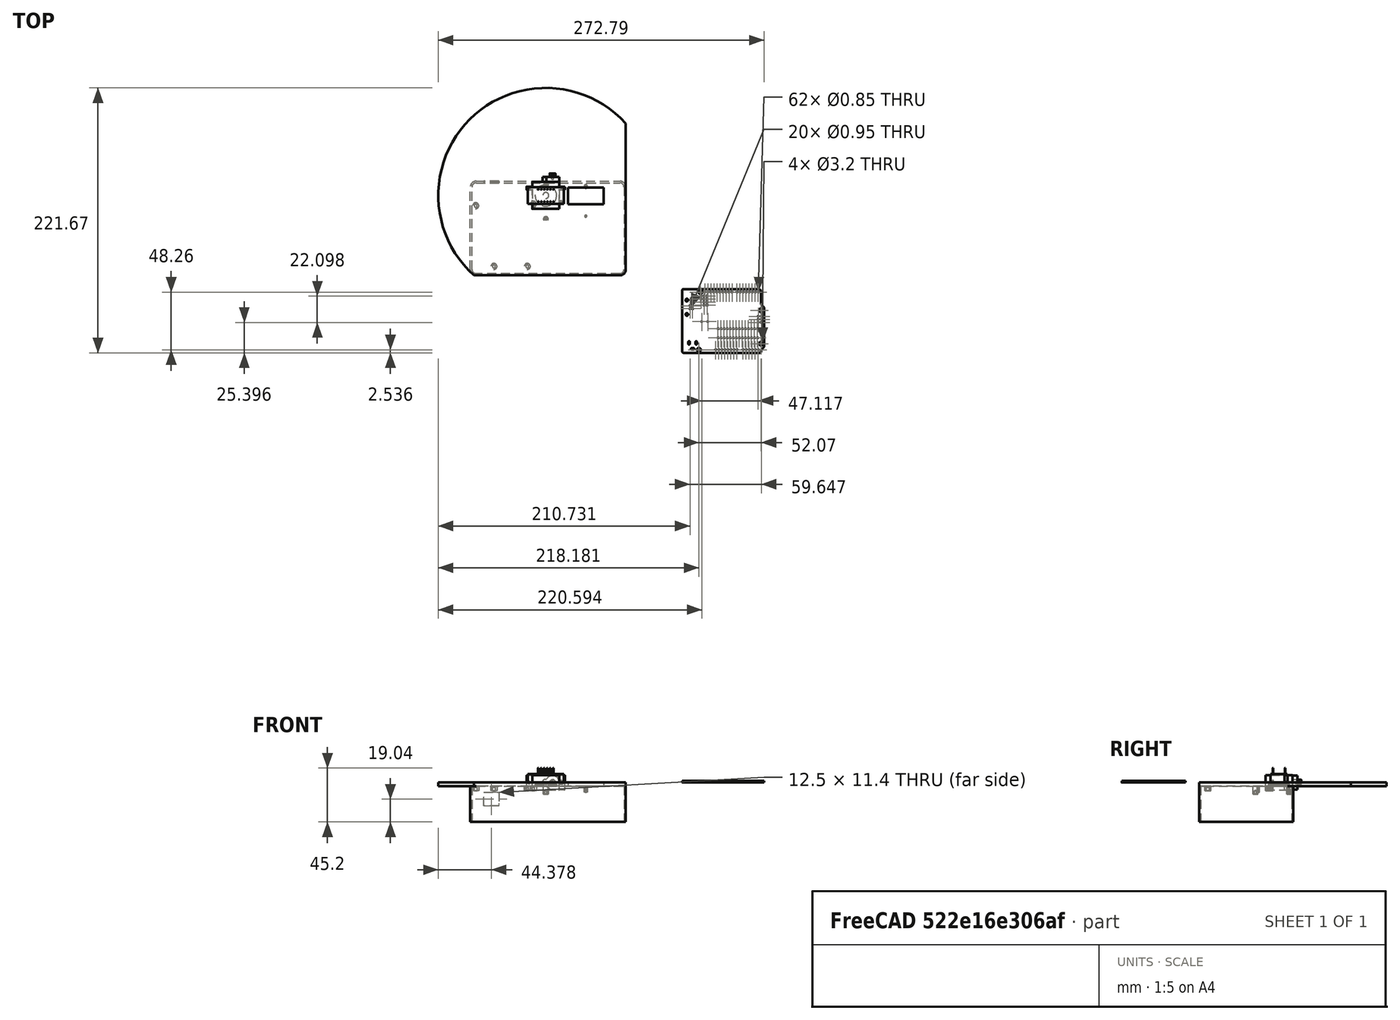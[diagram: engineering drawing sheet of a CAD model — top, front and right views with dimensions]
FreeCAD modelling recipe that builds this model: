
FCSTD DOCUMENT  (FreeCAD 1.0RUnknown)
Label: shell.FCStd.bak
License: All rights reserved
LicenseURL: https://en.wikipedia.org/wiki/All_rights_reserved
objects: App::FeaturePython×9, Sketcher::SketchObject×7, PartDesign::Pad×6, App::Link×4, Part::Feature×3, PartDesign::Hole×3, PartDesign::Pocket×2, App::Part×1, Assembly::JointGroup×1, Assembly::AssemblyObject×1, PartDesign::Body×1
note: 51 computed .brp shape members not serialized (recipe doc carries the construction recipe); baked Part::Feature solids carry a one-line shape summary decoded from their .brp

FEATURE [Sketcher::SketchObject] Sketch
  ArcFitTolerance = 1e-06
  AttachmentSupport = -> [XY_Plane]
  FullyConstrained = true
  MakeInternals = false
  MapMode = 5
  sketch-geometry (14):
    g0: LineSegment StartX=18.4415 StartY=6.5 StartZ=0 EndX=18.4415 EndY=-7.5 EndZ=0
    g1: LineSegment StartX=18.4415 StartY=-7.5 StartZ=0 EndX=48.4415 EndY=-7.5 EndZ=0
    g2: LineSegment StartX=48.4415 StartY=-7.5 StartZ=0 EndX=48.4415 EndY=6.5 EndZ=0
    g3: LineSegment StartX=48.4415 StartY=6.5 StartZ=0 EndX=18.4415 EndY=6.5 EndZ=0
    g4: GeomPoint [constr] X=33.4415 Y=-0.5 Z=0
    g5: ArcOfCircle CenterX=0 CenterY=0 CenterZ=0 NormalX=0 NormalY=0 NormalZ=1 AngleXU=0 Radius=90 StartAngle=0.733038 EndAngle=3.97935
    g6: Circle CenterX=0 CenterY=0 CenterZ=0 NormalX=0 NormalY=0 NormalZ=1 AngleXU=0 Radius=2.5
    g7: LineSegment [constr] StartX=0 StartY=0 StartZ=0 EndX=66.883 EndY=60.2218 EndZ=0
    g8: LineSegment [constr] StartX=0 StartY=0 StartZ=0 EndX=-60.2218 EndY=-66.883 EndZ=0
    g9: LineSegment StartX=66.883 StartY=60.2218 StartZ=0 EndX=66.883 EndY=-61.883 EndZ=0
    g10: LineSegment StartX=61.883 StartY=-66.883 StartZ=0 EndX=-60.2218 EndY=-66.883 EndZ=0
    g11: ArcOfCircle CenterX=61.883 CenterY=-61.883 CenterZ=0 NormalX=0 NormalY=0 NormalZ=1 AngleXU=0 Radius=5 StartAngle=4.71239 EndAngle=6.28319
    g12: LineSegment [constr] StartX=48.4415 StartY=3.78 StartZ=0 EndX=66.883 EndY=3.78 EndZ=0
    g13: LineSegment [constr] StartX=0 StartY=0 StartZ=0 EndX=18.4415 EndY=0 EndZ=0
  constraints (37):
    c: Coincident(g0,g1)
    c: Coincident(g1,g2)
    c: Coincident(g2,g3)
    c: Coincident(g3,g0)
    c: Vertical(g2)
    c: Horizontal(g1)
    c: Horizontal(g3)
    c: Symmetric(g2,g0,g4)
    c: DistanceX(g1,g1) = 30
    c: DistanceY(g2,g2) = 14
    c: Radius(g5) = 90
    c: Coincident(g5,g-1)
    c: Coincident(g6,g5)
    c: Diameter(g6) = 5
    c: Coincident(g7,g5)
    c: Coincident(g8,g5)
    c: Angle(g8,g-1,g5) = 2.30383
    c: Vertical(g9)
    c: Horizontal(g10)
    c: Angle(g-1,g7) = 0.733038
    c: Tangent(g9,g11) = 1.5708
    c: Tangent(g10,g11) = 1.5708
    c: Radius(g11) = 5
    c: Coincident(g5,g8)
    c: Coincident(g5,g7)
    c: Coincident(g9,g5)
    c: Coincident(g10,g5)
    c: PointOnObject(g12,g9)
    c: PointOnObject(g12,g2)
    c: DistanceY(g-1,g12) = 3.78
    c: Horizontal(g12,g12)
    c: Coincident(g13,g5)
    c: Vertical(g13,g0)
    c: PointOnObject(g13,g-1)
    c: Equal(g12,g13)
    c: Perpendicular(g0,g1)
    c: DistanceY(g-1,g4) = -0.5
FEATURE [PartDesign::Pad] Pad
  Direction = (0,0,1)
  Length = 3
  Length2 = 10
  Profile = -> Sketch
  ReferenceAxis = -> Sketch [N_Axis]
  Refine = true
  Reversed = true
  Suppressed = false
  Type = 0
FEATURE [Sketcher::SketchObject] Sketch001
  ArcFitTolerance = 1e-06
  FullyConstrained = true
  MakeInternals = false
  MapMode = 5
  Placement = pos=(0,0,-3) rot=(1,0,0;3.14159rad)
  sketch-geometry (1):
    g0: Circle CenterX=0 CenterY=0 CenterZ=0 NormalX=0 NormalY=0 NormalZ=1 AngleXU=0 Radius=9
  constraints (2):
    c: Diameter(g0) = 18
    c: Coincident(g0,g-1)
FEATURE [Sketcher::SketchObject] Sketch003
  ArcFitTolerance = 1e-06
  FullyConstrained = true
  MakeInternals = false
  MapMode = 5
  Placement = pos=(0,0,-3) rot=(1,0,0;3.14159rad)
  sketch-geometry (3):
    g0: Circle CenterX=1e-16 CenterY=19.72 CenterZ=0 NormalX=0 NormalY=0 NormalZ=1 AngleXU=0 Radius=2
    g1: Circle CenterX=0 CenterY=-8.53 CenterZ=0 NormalX=0 NormalY=0 NormalZ=1 AngleXU=0 Radius=2
    g2: LineSegment [constr] StartX=1e-16 StartY=19.72 StartZ=0 EndX=0 EndY=-8.53 EndZ=0
  constraints (8):
    c: Diameter(g0) = 4
    c: Diameter(g1) = 4
    c: Distance(g0,g1) = 28.25
    c: Distance(g1,g-1) = 8.53
    c: DistanceX(g1,g-1) = 0
    c: Coincident(g2,g0)
    c: Coincident(g2,g1)
    c: PointOnObject(g-1,g2)
FEATURE [PartDesign::Pocket] Pocket001
  BaseFeature = -> Pad
  Direction = (0,0,1)
  Length = 1.5
  Length2 = 5
  Profile = -> Sketch001
  ReferenceAxis = -> Sketch001 [N_Axis]
  Refine = true
  Suppressed = false
  Type = 0
FEATURE [Sketcher::SketchObject] Sketch002
  ArcFitTolerance = 1e-06
  AttachmentSupport = -> [Pocket001]
  ExternalGeometry = -> [Pocket001]
  FullyConstrained = true
  MakeInternals = false
  MapMode = 5
  Placement = pos=(0,0,-3) rot=(1,0,0;3.14159rad)
  sketch-geometry (5):
    g0: Circle CenterX=-43.4418 CenterY=59.423 CenterZ=0 NormalX=0 NormalY=0 NormalZ=1 AngleXU=0 Radius=2.5
    g1: Circle CenterX=-15.5018 CenterY=59.423 CenterZ=0 NormalX=0 NormalY=0 NormalZ=1 AngleXU=0 Radius=2.5
    g2: Circle CenterX=-10.4218 CenterY=7.35303 CenterZ=0 NormalX=0 NormalY=0 NormalZ=1 AngleXU=0 Radius=2.5
    g3: Circle CenterX=-58.6818 CenterY=8.62303 CenterZ=0 NormalX=0 NormalY=0 NormalZ=1 AngleXU=0 Radius=2.5
    g4: GeomPoint X=-61.2218 Y=-6.61697 Z=0
  constraints (14):
    c: Equal(g1,g0)
    c: Equal(g0,g3)
    c: Equal(g3,g2)
    c: Diameter(g3) = 5
    c: DistanceY(g4,g3) = 15.24
    c: DistanceY(g4,g0) = 66.04
    c: Horizontal(g0,g1)
    c: DistanceX(g4,g3) = 2.54
    c: DistanceX(g4,g2) = 50.8
    c: DistanceX(g4,g0) = 17.78
    c: DistanceX(g4,g1) = 45.72
    c: DistanceX(g4,g-3) = 1
    c: DistanceY(g4,g-3) = 73.5
    c: DistanceY(g4,g2) = 13.97
FEATURE [PartDesign::Pad] Pad005
  BaseFeature = -> Pocket001
  Direction = (0,0,-1)
  Length = 4
  Length2 = 10
  Profile = -> Sketch002
  ReferenceAxis = -> Sketch002 [N_Axis]
  Refine = true
  Suppressed = false
  Type = 0
FEATURE [PartDesign::Pad] Pad002
  BaseFeature = -> Pad005
  Direction = (0,-1e-16,-1)
  Length = 6.75
  Length2 = 10
  Profile = -> Sketch003
  ReferenceAxis = -> Sketch003 [N_Axis]
  Refine = true
  Suppressed = false
  Type = 0
FEATURE [Sketcher::SketchObject] Sketch005
  ArcFitTolerance = 1e-06
  ExternalGeometry = -> [Sketch002]
  FullyConstrained = true
  MakeInternals = false
  MapMode = 5
  Placement = pos=(0,12.03,0) rot=(0,0.707107,0.707107;3.14159rad)
  sketch-geometry (4):
    g0: LineSegment StartX=51.8718 StartY=-19.66 StartZ=0 EndX=51.8718 EndY=-8.26 EndZ=0
    g1: LineSegment StartX=51.8718 StartY=-8.26 StartZ=0 EndX=39.3718 EndY=-8.26 EndZ=0
    g2: LineSegment StartX=39.3718 StartY=-8.26 StartZ=0 EndX=39.3718 EndY=-19.66 EndZ=0
    g3: LineSegment StartX=39.3718 StartY=-19.66 StartZ=0 EndX=51.8718 EndY=-19.66 EndZ=0
  constraints (12):
    c: Coincident(g0,g1)
    c: Coincident(g1,g2)
    c: Coincident(g2,g3)
    c: Coincident(g3,g0)
    c: Vertical(g0)
    c: Vertical(g2)
    c: Horizontal(g1)
    c: Horizontal(g3)
    c: DistanceY(g1,g-3) = 5.26
    c: DistanceX(g0,g-3) = 9.35
    c: DistanceX(g1,g1) = 12.5
    c: DistanceY(g2,g2) = 11.4
FEATURE [App::Link] shell  label="shell001"
  LinkedObject = -> Body
FEATURE [App::FeaturePython] GroundedJoint  # Assembly grounded joint (typed FeaturePython)
  ObjectToGround = -> shell
FEATURE [Part::Feature] Part__Feature  label="SG90-SERVO"
  shape: bbox 32.25 x 29.75 x 12.5 mm, 92 faces (baked)
FEATURE [Part::Feature] Part__Feature001  label="Corps"
  shape: bbox 30 x 14 x 12.2 mm, 30 faces (baked)
FEATURE [Part::Feature] Part__Feature002  label="UNO-TH_Rev3e_PCB"
  shape: bbox 68.58 x 53.34 x 1.51 mm, 119 faces (baked)
FEATURE [App::Part] UNO_TH_Rev3e_1  label="UNO-TH_Rev3e 1"
  Group = -> [Part__Feature002]
  Origin = -> Origin002
FEATURE [App::Link] SG90_SERVO  label="SG90-SERVO001"
  LinkPlacement = pos=(-2.1e-15,-5.595,-17) rot=(0.57735,0.57735,0.57735;2.0944rad)
  LinkedObject = -> Part__Feature
  Placement = pos=(-2.1e-15,-5.595,-17) rot=(0.57735,0.57735,0.57735;2.0944rad)
FEATURE [App::Link] Corps  label="Corps001"
  LinkPlacement = pos=(33.4415,-0.5,0) rot=(1,0,0;3.14159rad)
  LinkedObject = -> Part__Feature001
  Placement = pos=(33.4415,-0.5,0) rot=(1,0,0;3.14159rad)
FEATURE [App::Link] UNO_TH_Rev3e_PCB  label="UNO-TH_Rev3e_PCB001"
  LinkPlacement = pos=(-139.439,120.908,-7) rot=(-0.706879,0.707335,0;3.14159rad)
  LinkedObject = -> Part__Feature002
  Placement = pos=(-139.439,120.908,-7) rot=(-0.706879,0.707335,0;3.14159rad)
FEATURE [App::FeaturePython] Joint  label="Longueur"  # Assembly joint (typed FeaturePython)
  Activated = true
  AngleMax = 0
  AngleMin = 0
  Detach1 = false
  Detach2 = false
  Distance = 0
  Distance2 = 0
  EnableAngleMax = false
  EnableAngleMin = false
  EnableLengthMax = false
  EnableLengthMin = false
  JointType = 5 (Distance)
  LengthMax = 0
  LengthMin = 0
  Placement1 = pos=(-13.6729,7.25,-7.24e-14) rot=(0,-0.707107,-0.707107;3.14159rad)
  Placement2 = pos=(-2e-16,-19.72,-9.75) rot=(0,0,1;1.5708rad)
  Reference1 = -> Assembly [SG90_SERVO.Face3,SG90_SERVO.Face3]
  Reference2 = -> Assembly [shell.Face47,shell.Face47]
FEATURE [App::FeaturePython] Joint001  label="Pivotglissant"  # Assembly joint (typed FeaturePython)
  Activated = true
  AngleMax = 0
  AngleMin = 0
  Detach1 = false
  Detach2 = false
  Distance = 0
  Distance2 = 0
  EnableAngleMax = false
  EnableAngleMin = false
  EnableLengthMax = false
  EnableLengthMin = false
  JointType = 2 (Cylindrical)
  LengthMax = 0
  LengthMin = 0
  Placement1 = pos=(-14.125,4.75,3.1e-15) rot=(-0.186157,-0.694747,-0.694747;2.77349rad)
  Placement2 = pos=(1e-16,-19.72,-9.75) rot=(0,1,0;3.14159rad)
  Reference1 = -> Assembly [SG90_SERVO.Edge57,SG90_SERVO.Edge57]
  Reference2 = -> Assembly [shell.Edge128,shell.Edge128]
FEATURE [App::FeaturePython] Joint002  label="Parallèle"  # Assembly joint (typed FeaturePython)
  Activated = true
  AngleMax = 0
  AngleMin = 0
  Detach1 = false
  Detach2 = false
  Distance = 0
  Distance2 = 0
  EnableAngleMax = false
  EnableAngleMin = false
  EnableLengthMax = false
  EnableLengthMin = false
  JointType = 6 (Parallel)
  LengthMax = 0
  LengthMin = 0
  Placement1 = pos=(16.125,6,3) rot=(-0.57735,-0.57735,-0.57735;4.18879rad)
  Placement2 = pos=(3.75822,10.53,-18.1663) rot=(1,0,0;1.5708rad)
  Reference1 = -> Assembly [SG90_SERVO.Face24,SG90_SERVO.Face24]
  Reference2 = -> Assembly [shell.Face21,shell.Face21]
FEATURE [App::FeaturePython] Joint003  label="Longueur001"  # Assembly joint (typed FeaturePython)
  Activated = true
  AngleMax = 0
  AngleMin = 0
  Detach1 = false
  Detach2 = false
  Distance = 0
  Distance2 = 0
  EnableAngleMax = false
  EnableAngleMin = false
  EnableLengthMax = false
  EnableLengthMin = false
  JointType = 5 (Distance)
  LengthMax = 0
  LengthMin = 0
  Placement2 = pos=(15,2e-16,3.6) rot=(-0.57735,-0.57735,0.57735;2.0944rad)
  Reference1 = -> Assembly [shell.?Face13,shell.?Face13]
  Reference2 = -> Assembly [Corps.Face3,Corps.Face3]
FEATURE [App::FeaturePython] Joint004  label="Longueur002"  # Assembly joint (typed FeaturePython)
  Activated = true
  AngleMax = 0
  AngleMin = 0
  Detach1 = false
  Detach2 = false
  Distance = 0
  Distance2 = 0
  EnableAngleMax = false
  EnableAngleMin = false
  EnableLengthMax = false
  EnableLengthMin = false
  JointType = 5 (Distance)
  LengthMax = 0
  LengthMin = 0
  Placement1 = pos=(0,4e-16,0) rot=(0,0,1;0rad)
  Reference1 = -> Assembly [Corps.Face4,Corps.Face4]
  Reference2 = -> Assembly [shell.?Face4,shell.?Face4]
FEATURE [App::FeaturePython] Joint006  label="Longueur003"  # Assembly joint (typed FeaturePython)
  Activated = true
  AngleMax = 0
  AngleMin = 0
  Detach1 = false
  Detach2 = false
  Distance = 0
  Distance2 = 0
  EnableAngleMax = false
  EnableAngleMin = false
  EnableLengthMax = false
  EnableLengthMin = false
  JointType = 5 (Distance)
  LengthMax = 0
  LengthMin = 0
  Placement1 = pos=(-10.4218,-7.35303,-7) rot=(0,0,1;1.5708rad)
  Placement2 = pos=(148.063,-105.106,0) rot=(0,0,1;0rad)
  Reference1 = -> Assembly [shell.Face46,shell.Face46]
  Reference2 = -> Assembly [UNO_TH_Rev3e_PCB.Face4,UNO_TH_Rev3e_PCB.Face4]
FEATURE [App::FeaturePython] Joint007  label="Parallèle001"  # Assembly joint (typed FeaturePython)
  Activated = true
  AngleMax = 0
  AngleMin = 0
  Detach1 = false
  Detach2 = false
  Distance = 0
  Distance2 = 0
  EnableAngleMax = false
  EnableAngleMin = false
  EnableLengthMax = false
  EnableLengthMin = false
  JointType = 6 (Parallel)
  LengthMax = 0
  LengthMin = 0
  Placement1 = pos=(148.063,-105.106,1.51) rot=(0,0,1;0rad)
  Placement2 = pos=(0.634359,-29.4883,-3) rot=(0,0,1;0rad)
  Reference1 = -> Assembly [UNO_TH_Rev3e_PCB.Face5,UNO_TH_Rev3e_PCB.Face5]
  Reference2 = -> Assembly [shell.Face27,shell.Face27]
FEATURE [App::FeaturePython] Joint008  label="Pivotglissant001"  # Assembly joint (typed FeaturePython)
  Activated = true
  AngleMax = 0
  AngleMin = 0
  Detach1 = false
  Detach2 = false
  Distance = 0
  Distance2 = 0
  EnableAngleMax = false
  EnableAngleMin = false
  EnableLengthMax = false
  EnableLengthMin = false
  JointType = 2 (Cylindrical)
  LengthMax = 0
  LengthMin = 0
  Placement2 = pos=(180.251,-124.054,0.755) rot=(0.707107,-0.707107,0;3.14159rad)
  Reference1 = -> Assembly [shell.?Face52,shell.?Face52]
  Reference2 = -> Assembly [UNO_TH_Rev3e_PCB.Face64,UNO_TH_Rev3e_PCB.Face64]
FEATURE [Assembly::JointGroup] Joints
  Group = -> [GroundedJoint,Joint,Joint001,Joint002,Joint003,Joint004,Joint006,Joint007,Joint008]
FEATURE [Assembly::AssemblyObject] Assembly
  Group = -> [Joints,shell,GroundedJoint,SG90_SERVO,Corps,UNO_TH_Rev3e_PCB,Joint,Joint001,Joint002,Joint003,Joint004,Joint006,Joint007,Joint008]
  Origin = -> Origin001
  Type = Assembly
FEATURE [PartDesign::Hole] Hole001
  BaseFeature = -> Pad002
  CustomThreadClearance = 0
  Depth = 3
  DepthType = 0
  Diameter = 1.6
  DrillForDepth = false
  DrillPoint = 1
  DrillPointAngle = 118
  HoleCutCountersinkAngle = 90
  HoleCutCustomValues = false
  HoleCutDepth = 0
  HoleCutDiameter = 6.1
  HoleCutType = 0
  ModelThread = false
  Profile = -> Pad002 [Face26,Face24]
  Refine = true
  Suppressed = false
  Tapered = false
  TaperedAngle = 90
  ThreadClass = 0
  ThreadDepth = 3
  ThreadDepthType = 0
  ThreadDirection = 0
  ThreadFit = 0
  ThreadSize = 6
  ThreadType = 1
  Threaded = true
  UseCustomThreadClearance = false
FEATURE [PartDesign::Pad] Pad003
  BaseFeature = -> Hole001
  Direction = (0,-1e-16,-1)
  Length = 3
  Length2 = 10
  Profile = -> Sketch003 [Edge2]
  ReferenceAxis = -> Sketch003 [N_Axis]
  Refine = true
  Reversed = true
  Suppressed = false
  Type = 0
FEATURE [Sketcher::SketchObject] Sketch004
  ArcFitTolerance = 1e-06
  AttachmentSupport = -> [Pad003]
  ExternalGeometry = -> [Pad003]
  FullyConstrained = true
  MakeInternals = false
  MapMode = 5
  Placement = pos=(0,0,-3) rot=(1,0,0;3.14159rad)
  sketch-geometry (22):
    g0: LineSegment StartX=-63.2708 StartY=61.883 StartZ=0 EndX=-63.2708 EndY=-7.03 EndZ=0
    g1: LineSegment StartX=-58.2708 StartY=-12.03 StartZ=0 EndX=61.883 EndY=-12.03 EndZ=0
    g2: LineSegment StartX=66.883 StartY=-7.03 StartZ=0 EndX=66.883 EndY=61.883 EndZ=0
    g3: LineSegment StartX=61.883 StartY=66.883 StartZ=0 EndX=-58.2708 EndY=66.883 EndZ=0
    g4: ArcOfCircle CenterX=61.883 CenterY=61.883 CenterZ=0 NormalX=0 NormalY=0 NormalZ=1 AngleXU=0 Radius=5 StartAngle=3.1571e-08 EndAngle=1.5708
    g5: LineSegment StartX=-61.7708 StartY=61.883 StartZ=0 EndX=-61.7708 EndY=-7.03 EndZ=0
    g6: LineSegment StartX=-58.2708 StartY=-10.53 StartZ=0 EndX=61.883 EndY=-10.53 EndZ=0
    g7: LineSegment StartX=65.383 StartY=-7.03 StartZ=0 EndX=65.383 EndY=61.883 EndZ=0
    g8: LineSegment StartX=61.883 StartY=65.383 StartZ=0 EndX=-58.2708 EndY=65.383 EndZ=0
    g9: ArcOfCircle CenterX=61.883 CenterY=61.883 CenterZ=0 NormalX=0 NormalY=0 NormalZ=1 AngleXU=0 Radius=3.5 StartAngle=4e-16 EndAngle=1.5708
    g10: GeomPoint [constr] X=65.383 Y=65.383 Z=0
    g11: ArcOfCircle CenterX=-58.2708 CenterY=-7.03 CenterZ=0 NormalX=0 NormalY=0 NormalZ=1 AngleXU=0 Radius=3.5 StartAngle=3.14159 EndAngle=4.71239
    g12: GeomPoint [constr] X=-61.7708 Y=-10.53 Z=0
    g13: ArcOfCircle CenterX=-58.2708 CenterY=-7.03 CenterZ=0 NormalX=0 NormalY=0 NormalZ=1 AngleXU=0 Radius=5 StartAngle=3.14159 EndAngle=4.71239
    g14: GeomPoint [constr] X=-63.2708 Y=-12.03 Z=0
    g15: ArcOfCircle CenterX=61.883 CenterY=-7.03 CenterZ=0 NormalX=0 NormalY=0 NormalZ=1 AngleXU=0 Radius=3.5 StartAngle=4.71239 EndAngle=6.28319
    g16: GeomPoint [constr] X=65.383 Y=-10.53 Z=0
    g17: ArcOfCircle CenterX=61.883 CenterY=-7.03 CenterZ=0 NormalX=0 NormalY=0 NormalZ=1 AngleXU=0 Radius=5 StartAngle=4.71239 EndAngle=6.28319
    g18: GeomPoint [constr] X=66.883 Y=-12.03 Z=0
    g19: ArcOfCircle CenterX=-58.2708 CenterY=61.883 CenterZ=0 NormalX=0 NormalY=0 NormalZ=1 AngleXU=0 Radius=3.5 StartAngle=1.5708 EndAngle=3.14159
    g20: GeomPoint [constr] X=-61.7708 Y=65.383 Z=0
    g21: ArcOfCircle CenterX=-58.2708 CenterY=61.883 CenterZ=0 NormalX=0 NormalY=0 NormalZ=1 AngleXU=0 Radius=5 StartAngle=1.5708 EndAngle=3.14159
  constraints (52):
    c: PointOnObject(g18,g-4)
    c: Horizontal(g1)
    c: Perpendicular(g0,g1)
    c: Coincident(g4,g3)
    c: Coincident(g-5,g4)
    c: Coincident(g4,g2)
    c: Coincident(g-5,g3)
    c: DistanceX(g2,g-5) = 0
    c: Vertical(g5)
    c: Vertical(g7)
    c: Horizontal(g6)
    c: Horizontal(g8)
    c: Distance(g3,g8) = 1.5
    c: Distance(g14,g6) = 1.5
    c: Tangent(g6,g-6)
    c: Distance(g18,g7) = 1.5
    c: PointOnObject(g10,g8)
    c: PointOnObject(g10,g7)
    c: Tangent(g8,g9) = -1.5708
    c: Tangent(g7,g9) = -1.5708
    c: Distance(g4,g9) = 1.5
    c: PointOnObject(g12,g6)
    c: PointOnObject(g12,g5)
    c: Tangent(g6,g11) = -1.5708
    c: Tangent(g5,g11) = -1.5708
    c: PointOnObject(g14,g1)
    c: PointOnObject(g14,g0)
    c: Tangent(g1,g13) = -1.5708
    c: Tangent(g0,g13) = -1.5708
    c: Vertical(g6,g1)
    c: Distance(g11,g13) = 5
    c: PointOnObject(g16,g6)
    c: PointOnObject(g16,g7)
    c: Tangent(g6,g15) = -1.5708
    c: Tangent(g7,g15) = -1.5708
    c: PointOnObject(g18,g1)
    c: PointOnObject(g18,g2)
    c: Tangent(g1,g17) = -1.5708
    c: Tangent(g2,g17) = -1.5708
    c: Vertical(g1,g6)
    c: Distance(g15,g17) = 5
    c: PointOnObject(g20,g8)
    c: PointOnObject(g20,g5)
    c: Tangent(g8,g19) = -1.5708
    c: Tangent(g5,g19) = -1.5708
    c: Tangent(g3,g21) = -1.5708
    c: Tangent(g0,g21) = -1.5708
    c: Vertical(g8,g3)
    c: Horizontal(g5,g0)
    c: Distance(g21,g19) = 1.5
    c: Distance(g19,g21) = 5
    c: Tangent(g21,g-7)
FEATURE [PartDesign::Pad] Pad006
  BaseFeature = -> Pad003
  Direction = (0,0,-1)
  Length = 30
  Length2 = 10
  Profile = -> Sketch004
  ReferenceAxis = -> Sketch004 [N_Axis]
  Refine = true
  Suppressed = false
  Type = 0
FEATURE [PartDesign::Pocket] Pocket
  BaseFeature = -> Pad006
  Direction = (-1e-16,-1,2e-16)
  Length = 5
  Length2 = 5
  Profile = -> Sketch005
  ReferenceAxis = -> Sketch005 [N_Axis]
  Refine = true
  Suppressed = false
  Type = 0
FEATURE [PartDesign::Hole] Hole
  BaseFeature = -> Pocket
  CustomThreadClearance = 0
  Depth = 3
  DepthType = 0
  Diameter = 2.4
  DrillForDepth = false
  DrillPoint = 1
  DrillPointAngle = 118
  HoleCutCountersinkAngle = 90
  HoleCutCustomValues = false
  HoleCutDepth = 0
  HoleCutDiameter = 6.1
  HoleCutType = 0
  ModelThread = false
  Profile = -> Pocket [Face42,Face40,Face41,Face44]
  Refine = true
  Suppressed = false
  Tapered = false
  TaperedAngle = 90
  ThreadClass = 0
  ThreadDepth = 3
  ThreadDepthType = 0
  ThreadDirection = 0
  ThreadFit = 0
  ThreadSize = 6
  ThreadType = 1
  Threaded = false
  UseCustomThreadClearance = false
FEATURE [Sketcher::SketchObject] Sketch006
  ArcFitTolerance = 1e-06
  AttachmentSupport = -> [Pad006]
  ExternalGeometry = -> [Pad006]
  FullyConstrained = true
  MakeInternals = false
  MapMode = 5
  Placement = pos=(0,0,-3) rot=(1,0,0;3.14159rad)
  sketch-geometry (2):
    g0: Circle CenterX=33.4415 CenterY=-7.7 CenterZ=0 NormalX=0 NormalY=0 NormalZ=1 AngleXU=0 Radius=1.3
    g1: Circle CenterX=33.4415 CenterY=17.3 CenterZ=0 NormalX=0 NormalY=0 NormalZ=1 AngleXU=0 Radius=0.9
  constraints (6):
    c: Diameter(g0) = 2.6
    c: Diameter(g1) = 1.8
    c: DistanceX(g-3,g0) = 15
    c: Vertical(g1,g0)
    c: DistanceY(g0,g1) = 25
    c: Distance(g0,g-3) = 1.2
FEATURE [PartDesign::Pad] Pad007
  BaseFeature = -> Hole
  Direction = (0,0,-1)
  Length = 5
  Length2 = 10
  Profile = -> Sketch006
  ReferenceAxis = -> Sketch006 [N_Axis]
  Refine = true
  Suppressed = false
  Type = 0
FEATURE [PartDesign::Hole] Hole002
  BaseFeature = -> Pad007
  CustomThreadClearance = 0
  Depth = 3
  DepthType = 0
  Diameter = 1.2
  DrillForDepth = false
  DrillPoint = 1
  DrillPointAngle = 118
  HoleCutCountersinkAngle = 90
  HoleCutCustomValues = false
  HoleCutDepth = 0
  HoleCutDiameter = 6.1
  HoleCutType = 0
  ModelThread = false
  Profile = -> Pad007 [Face48,Face50]
  Refine = true
  Suppressed = false
  Tapered = false
  TaperedAngle = 90
  ThreadClass = 0
  ThreadDepth = 3
  ThreadDepthType = 0
  ThreadDirection = 0
  ThreadFit = 0
  ThreadSize = 0
  ThreadType = 1
  Threaded = false
  UseCustomThreadClearance = false
FEATURE [PartDesign::Body] Body  label="shell"
  AllowCompound = false
  Group = -> [Sketch,Pad,Sketch001,Pocket001,Sketch002,Pad005,Sketch003,Pad002,Hole001,Pad003,Sketch004,Pad006,Sketch005,Pocket,Hole,Sketch006,Pad007,Hole002]
  Origin = -> Origin
  Tip = -> Hole002
